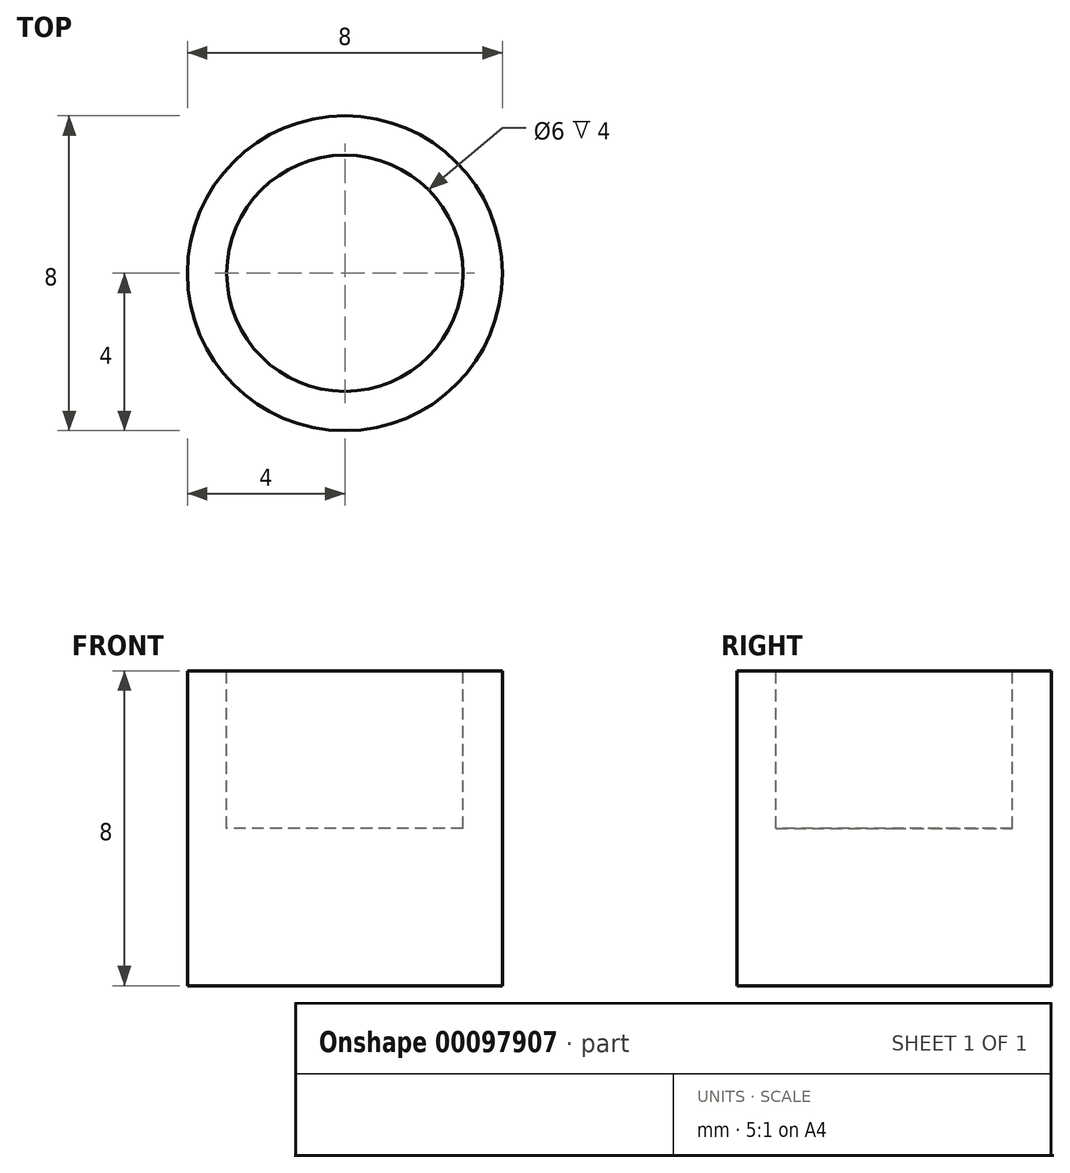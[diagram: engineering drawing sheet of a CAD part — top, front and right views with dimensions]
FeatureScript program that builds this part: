
annotation { "Feature Type Name" : "Feature", "Feature Type Description" : "" }
export const myFeature = defineFeature(function(context is Context, id is Id, definition is map)
    precondition{}
    {
        {
            var Q0;
            Q0=qCreatedBy(makeId("Top.planeOp"),FACE);
            var sketch = newSketch(context, id + "F0", { "sketchPlane" : qUnion([Q0])});
            skCircle(sketch, "E0", {"center": v(0, 0) * mm, "radius": 4 * mm});
            skSolve(sketch);
        }
        {
            var Q0;
            Q0=makeQuery(id+"F0.imprint","IMPRINT",FACE,{"disambiguationData":[TD([[makeQuery(id+"F0.imprint","IMPRINT",EDGE,{"derivedFrom":sQuery(id+"F0.wireOp",EDGE,"E0")}),1.0]])]});
            extrude(context, id + "F1", {"entities" : qUnion([Q0]), "depth" : 8 * mm});
        }
        {
            var Q0;
            Q0=makeQuery(id+"F1.opExtrude","CAP_FACE",FACE,{"disambiguationData":[OSD([sQuery(id+"F0.wireOp",EDGE,"E0")])],"isStart":false});
            var sketch = newSketch(context, id + "F2", { "sketchPlane" : qUnion([Q0])});
            skLineSegment(sketch, "E1.bottom", {"start": v(-3, 3) * mm, "end": v(3, 3) * mm});
            skLineSegment(sketch, "E1.top", {"start": v(-3, -3) * mm, "end": v(3, -3) * mm});
            skLineSegment(sketch, "E1.left", {"start": v(-3, 3) * mm, "end": v(-3, -3) * mm});
            skLineSegment(sketch, "E1.right", {"start": v(3, 3) * mm, "end": v(3, -3) * mm});
            skCircle(sketch, "E2", {"center": v(0, 0) * mm, "radius": 3 * mm});
            skSolve(sketch);
        }
        {
            var Q0;
            {var subQ0=sQuery(id+"F2.wireOp",EDGE,"E2");var subQ1=makeQuery(id+"F2.imprint","INTERSECT",VERTEX,{"derivedFrom":[sQuery(id+"F2.wireOp",EDGE,"E1.bottom"),subQ0]});Q0=makeQuery(id+"F2.imprint","IMPRINT",FACE,{"disambiguationData":[TD([[makeQuery(id+"F2.imprint","IMPRINT",EDGE,{"disambiguationData":[TD([[subQ1,1.0]])],"derivedFrom":subQ0}),1.0]])]});}
            extrude(context, id + "F3", {"entities" : qUnion([Q0]), "operationType" : NewBodyOperationType.REMOVE, "oppositeDirection" : true, "depth" : 4 * mm});
        }
    });
